# Revit family: ledlima_l12-30w-4000-ble2_542003132000
name_source: partatom
category: Leuchten
revit_build: Autodesk Revit 2016 (Build: 20190508_0715(x64)
units: mm (PartAtom-declared; Revit-internal decimal feet)

## family parameters
Basisbauteil = Fläche
Beim Laden mit Abzugskörper schneiden = Nein
Bemaßung runder Anschluss = Durchmesser verwenden
Gemeinsam genutzt = Nein
Lichtquelle = Nein
Raumberechnungspunkt = Nein
Teiletyp = Normal

## types (1)
- LEDLima L12-30W-4000-BLE2 (1 x LED, 3450 lm, 4000)
    Approval mark = CE, ENEC
    Beschreibung = Stylish linear luminaire with high quality aluminum housing, suitable for surface mounting and suspended use. Suspension kit including transparent cable as accessory. Connection kit accessory to create continuous lines available.
    CIE Flux Codes = 68 91 98 100 100
    Color Rendering = 80
    Color Temperature = 4000
    Control Gear = Electronic ballast
    Frequency = 60 Hz
    Height = 75 mm
    Hersteller = OPPLE
    Lamp Light Flux = 3450 lm
    Lamp count = 1
    Lampe = 1 x LED
    Length = 1200 mm
    Luminous efficacy = 115 lm/W
    ModVariant = Nein
    Modell = 542003132000
    Mounting Place = Ceiling, Pole
    Mounting Type = Recessed, Pendant
    Number of Poles = 1
    OnlyDefault = Ja
    Power Factor = 1
    Product Name = LEDLima L12-30W-4000-BLE2
    Product group = Ceiling / wall-mounted luminaires
    ProductGroupID = 30
    Protection Class = Protection class I
    Protection Degree = IP 20
    RLX_Detail_Level = 1
    RlxData = <blob elided: 79453 chars, md5=33981571>
    Scheinlast = 30 VA
    Socket = socket
    Standby Power = 0 W
    System Light Flux = 3450 lm
    System Power = 30 W
    Typenbild = lima.jpg
    Typenkommentare = Product without accessories
    URL = http://relux.com
    VarID = ---
    Voltage = 230 V
    Voltage Range = 220-240 V
    Vorgabe-Ansicht = 1800 mm
    Weight = 0.00 kg
    Width = 70 mm

## geometry (parser evidence)
native form markers: Blend x4, Sweep x10
no freeform markers — native parametric forms only
